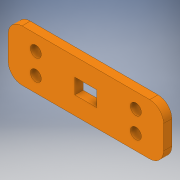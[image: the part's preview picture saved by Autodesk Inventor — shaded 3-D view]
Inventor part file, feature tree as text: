
AUTODESK INVENTOR PART (.ipt)
format: ipt  version: 2017 (Build 210142000, 142)  size: 138,752 bytes
history: native  units: in
note: dims shown in document units (in); Inventor stores cm internally (conversion verified against a paired STEP export)
features: sketch x3, extrude x2, hole x1, plane x1, mirror x1, fillet x1
ambient origin geometry x8: Origin, YZ Plane, XZ Plane, XY Plane, X Axis, Y Axis, Z Axis, Center Point
bodies: Solid1 (feature_tree)
feature tree (9):
  extrude  "Extrusion1"  Depth=0.93in
  hole  "Hole2"  [1 undecoded]
  plane  "Work Plane1"
  mirror  "Mirror1"
  extrude  "Extrusion2"  Depth=0.25in
  fillet  "Fillet1"  Radius=0.501in
  sketch  "Sketch1"  dims[d0=2.813in d1=0.93in]
  sketch  "Sketch3"  dims[d2=0.15in d3=0.0in d15=0.275in]
  sketch  "Sketch4"  dims[d16=0.275in d17=0.501in d18=0.501in d19=0.2in d20=0.75in d21=0.375in d22=0.25in d23=0.5635in d24=1.0in d25=0.8108in d26=0.4in d27=0.28in d28=2.813in d29=1.2065in d30=0.325in d31=0.93in d32=0.15in d33=0.0in d34=0.25in]
note: 1 required parameter value undecoded (feature->parameter linkage not recoverable at this tier; creation-order binding heuristic only, values carry confidence <= 0.55)
